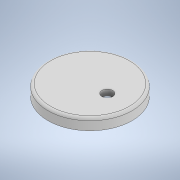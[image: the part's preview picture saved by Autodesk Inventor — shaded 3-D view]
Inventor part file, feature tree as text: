
AUTODESK INVENTOR PART (.ipt)
format: ipt  version: 2022 (Build 260153000, 153)  size: 151,040 bytes
history: native  units: in
note: dims shown in document units (in); Inventor stores cm internally (conversion verified against a paired STEP export)
features: sketch x3, extrude x2, revolve x1, fillet x1
ambient origin geometry x8: Origin, YZ Plane, XZ Plane, XY Plane, X Axis, Y Axis, Z Axis, Center Point
bodies: Solid1 (feature_tree)
feature tree (7):
  revolve  "Revolution1"  [1 undecoded]
  fillet  "Fillet1"  Radius=0.2362in
  extrude  "Extrusion1"  Depth=0.1575in
  extrude  "Extrusion2"  TaperAngle=90.0deg  [1 undecoded]
  sketch  "Sketch2"  dims[d0=1.9114in d1=0.1575in d2=0.2362in]
  sketch  "Sketch3"  dims[d3=0.5118in d4=0.1575in]
  sketch  "Sketch5"  dims[d5=0.2756in d6=90.0deg d7=0.1181in d8=1.3386in d9=0.7874in d11=360.0deg d13=0.1969in d14=0.0in d15=0.7697in d16=0.4921in d17=0.7874in d18=0.0in d19=0.0in]
note: 2 required parameter values undecoded (feature->parameter linkage not recoverable at this tier; creation-order binding heuristic only, values carry confidence <= 0.55)